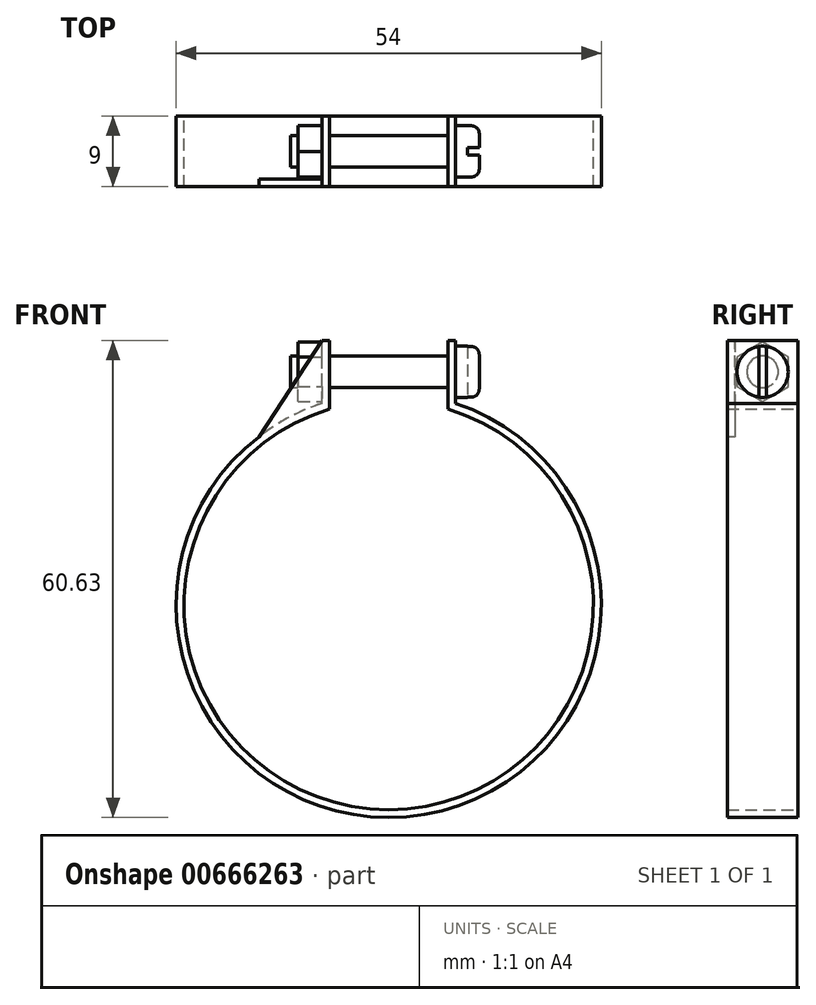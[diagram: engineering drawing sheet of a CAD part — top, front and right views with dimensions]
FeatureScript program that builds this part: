
annotation { "Feature Type Name" : "Feature", "Feature Type Description" : "" }
export const myFeature = defineFeature(function(context is Context, id is Id, definition is map)
    precondition{}
    {
        {
            var Q0;
            Q0=qCreatedBy(makeId("Front.planeOp"),FACE);
            var sketch = newSketch(context, id + "F0", { "sketchPlane" : qUnion([Q0])});
            skArc(sketch, "E0", {"start": v(-8.5, 25.63) * mm, "mid": v(0, -27) * mm, "end": v(8.5, 25.63) * mm});
            skArc(sketch, "E1", {"start": v(-7.5, 24.9) * mm, "mid": v(0, -26) * mm, "end": v(7.5, 24.9) * mm});
            skLineSegment(sketch, "E2", {"start": v(-8.5, 25.63) * mm, "end": v(-8.5, 33.63) * mm});
            skLineSegment(sketch, "E3", {"start": v(-8.5, 33.63) * mm, "end": v(-7.5, 33.63) * mm});
            skLineSegment(sketch, "E4", {"start": v(-7.5, 33.63) * mm, "end": v(-7.5, 24.9) * mm});
            skLineSegment(sketch, "E5", {"start": v(7.5, 24.9) * mm, "end": v(7.5, 33.63) * mm});
            skLineSegment(sketch, "E6", {"start": v(7.5, 33.63) * mm, "end": v(8.5, 33.63) * mm});
            skLineSegment(sketch, "E7", {"start": v(8.5, 33.63) * mm, "end": v(8.5, 25.63) * mm});
            skSolve(sketch);
        }
        {
            var Q0;
            Q0 = qSketchRegion(id + "F0", true);
            extrude(context, id + "F1", {"entities" : qUnion([Q0]), "depth" : 9 * mm, "offsetDistance" : 25 * mm, "symmetric" : true});
        }
        {
            var Q0;
            Q0=makeQuery(id+"F1.opExtrude","CAP_FACE",FACE,{"disambiguationData":[OSD([sQuery(id+"F0.wireOp",EDGE,"E0"),sQuery(id+"F0.wireOp",EDGE,"E1"),sQuery(id+"F0.wireOp",EDGE,"E2"),sQuery(id+"F0.wireOp",EDGE,"E3"),sQuery(id+"F0.wireOp",EDGE,"E4"),sQuery(id+"F0.wireOp",EDGE,"E5"),sQuery(id+"F0.wireOp",EDGE,"E6"),sQuery(id+"F0.wireOp",EDGE,"E7")])],"isStart":false});
            var sketch = newSketch(context, id + "F2", { "sketchPlane" : qUnion([Q0])});
            skLineSegment(sketch, "E8", {"start": v(-8.5, 33.63) * mm, "end": v(-16.5, 21.37) * mm});
            skLineSegment(sketch, "E9", {"start": v(-8.5, 25.63) * mm, "end": v(-8.5, 33.63) * mm});
            skArc(sketch, "E10", {"start": v(-8.5, 25.63) * mm, "mid": v(-12.68, 23.84) * mm, "end": v(-16.5, 21.37) * mm});
            skSolve(sketch);
        }
        {
            var Q0;
            Q0 = qSketchRegion(id + "F2", true);
            extrude(context, id + "F3", {"entities" : qUnion([Q0]), "operationType" : NewBodyOperationType.ADD, "oppositeDirection" : true, "depth" : 1 * mm, "offsetDistance" : 25 * mm});
        }
        {
            var Q0;
            Q0=makeQuery(id+"F1.opExtrude","SWEPT_FACE",FACE,{"disambiguationData":[OSD([sQuery(id+"F0.wireOp",EDGE,"E2")])]});
            var sketch = newSketch(context, id + "F4", { "sketchPlane" : qUnion([Q0])});
            skCircle(sketch, "E11.cCircle", {"center": v(0, 29.63) * mm, "radius": 3.25 * mm, "construction": true});
            skLineSegment(sketch, "E11.0", {"start": v(-3.25, 27.75) * mm, "end": v(-3.25, 31.5) * mm});
            skLineSegment(sketch, "E11.1", {"start": v(-3.25, 31.5) * mm, "end": v(0, 33.38) * mm});
            skLineSegment(sketch, "E11.2", {"start": v(0, 33.38) * mm, "end": v(3.25, 31.5) * mm});
            skLineSegment(sketch, "E11.3", {"start": v(3.25, 31.5) * mm, "end": v(3.25, 27.75) * mm});
            skLineSegment(sketch, "E11.4", {"start": v(3.25, 27.75) * mm, "end": v(0, 25.87) * mm});
            skLineSegment(sketch, "E11.5", {"start": v(0, 25.87) * mm, "end": v(-3.25, 27.75) * mm});
            skPoint(sketch, "E11.0.midPoint", {"position": v(-3.25, 29.63) * mm});
            skLineSegment(sketch, "E12", {"start": v(0, 33.63) * mm, "end": v(0, 25.63) * mm, "construction": true});
            skSolve(sketch);
        }
        {
            var Q0;
            Q0 = qSketchRegion(id + "F4", true);
            extrude(context, id + "F5", {"entities" : qUnion([Q0]), "operationType" : NewBodyOperationType.ADD, "depth" : 3 * mm, "offsetDistance" : 25 * mm});
        }
        {
            var Q0;
            Q0=makeQuery(id+"F1.opExtrude","SWEPT_FACE",FACE,{"disambiguationData":[OSD([sQuery(id+"F0.wireOp",EDGE,"E7")])]});
            var sketch = newSketch(context, id + "F6", { "sketchPlane" : qUnion([Q0])});
            skCircle(sketch, "E13", {"center": v(0, 29.63) * mm, "radius": 3.25 * mm});
            skSolve(sketch);
        }
        {
            var Q0;
            Q0 = qSketchRegion(id + "F6", true);
            extrude(context, id + "F7", {"entities" : qUnion([Q0]), "operationType" : NewBodyOperationType.ADD, "depth" : 3 * mm, "offsetDistance" : 25 * mm});
        }
        {
            var Q0;
            Q0=makeQuery(id+"F1.opExtrude","SWEPT_FACE",FACE,{"disambiguationData":[OSD([sQuery(id+"F0.wireOp",EDGE,"E5")])]});
            var sketch = newSketch(context, id + "F8", { "sketchPlane" : qUnion([Q0])});
            skCircle(sketch, "E14", {"center": v(0, 29.63) * mm, "radius": 2 * mm});
            skSolve(sketch);
        }
        {
            var Q0;
            Q0 = qSketchRegion(id + "F8", true);
            extrude(context, id + "F9", {"entities" : qUnion([Q0]), "operationType" : NewBodyOperationType.ADD, "depth" : 20 * mm, "offsetDistance" : 25 * mm});
        }
        {
            var Q0;
            Q0=makeQuery(id+"F7.opExtrude","CAP_FACE",FACE,{"disambiguationData":[OSD([sQuery(id+"F6.wireOp",EDGE,"E13")])],"isStart":false});
            var sketch = newSketch(context, id + "F10", { "sketchPlane" : qUnion([Q0])});
            skLineSegment(sketch, "E15.bottom", {"start": v(-0.5, 32.88) * mm, "end": v(0.5, 32.88) * mm});
            skLineSegment(sketch, "E15.top", {"start": v(-0.5, 26.38) * mm, "end": v(0.5, 26.38) * mm});
            skLineSegment(sketch, "E15.left", {"start": v(-0.5, 32.88) * mm, "end": v(-0.5, 26.38) * mm});
            skLineSegment(sketch, "E15.right", {"start": v(0.5, 32.88) * mm, "end": v(0.5, 26.38) * mm});
            skPoint(sketch, "E15.middle", {"position": v(0, 29.63) * mm});
            skSolve(sketch);
        }
        {
            var Q0;
            Q0 = qSketchRegion(id + "F10", true);
            extrude(context, id + "F11", {"entities" : qUnion([Q0]), "operationType" : NewBodyOperationType.REMOVE, "oppositeDirection" : true, "depth" : 1.5 * mm, "offsetDistance" : 25 * mm});
        }
        {
            var Q0;
            {var subQ0=sQuery(id+"F6.wireOp",EDGE,"E13");Q0=makeQuery(id+"F11.boolean.opBoolean","SPLIT",EDGE,{"disambiguationData":[TD([makeQuery(id+"F11.opExtrude","SWEPT_FACE",FACE,{"disambiguationData":[OSD([sQuery(id+"F10.wireOp",EDGE,"E15.left")])]})])],"derivedFrom":makeQuery(id+"F7.opExtrude","CAP_EDGE",EDGE,{"disambiguationData":[OSD([subQ0])],"isStart":false})});}
            var Q1;
            {var subQ0=sQuery(id+"F6.wireOp",EDGE,"E13");Q1=makeQuery(id+"F11.boolean.opBoolean","SPLIT",EDGE,{"disambiguationData":[TD([makeQuery(id+"F11.opExtrude","SWEPT_FACE",FACE,{"disambiguationData":[OSD([sQuery(id+"F10.wireOp",EDGE,"E15.right")])]})])],"derivedFrom":makeQuery(id+"F7.opExtrude","CAP_EDGE",EDGE,{"disambiguationData":[OSD([subQ0])],"isStart":false})});}
            fillet(context, id + "F12", {"entities" : qUnion([Q0, Q1]), "radius" : 1 * mm, "tangentPropagation" : true, "allowEdgeOverflow" : false});
        }
    });
